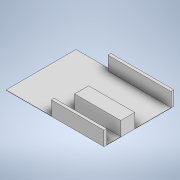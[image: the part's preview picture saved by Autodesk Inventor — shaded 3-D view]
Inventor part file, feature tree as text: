
AUTODESK INVENTOR PART (.ipt)
format: ipt  version: 2020 (Build 240168000, 168)  size: 119,296 bytes
history: native  units: mm
features: extrude x2, sketch x2
ambient origin geometry x8: Origin, YZ Plane, XZ Plane, XY Plane, X Axis, Y Axis, Z Axis, Center Point
bodies: Body1 (feature_tree)
feature tree (4):
  extrude  "Extrusão2"  Depth=50.0mm
  extrude  "Extrusão3"  Depth=45.0mm
  sketch  "Esboço3"  dims[d4=70.0mm d5=50.0mm]
  sketch  "Esboço4"  dims[d6=0.2mm d7=0.0mm d8=45.0mm d9=2.0mm d10=37.5mm d11=2.0mm d12=10.0mm d13=33.0mm d14=10.0mm d15=10.0mm d16=0.0mm]
